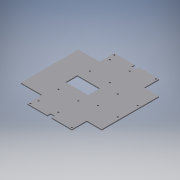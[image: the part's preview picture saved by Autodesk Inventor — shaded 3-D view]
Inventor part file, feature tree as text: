
AUTODESK INVENTOR PART (.ipt)
format: ipt  version: 2016 (Build 200138000, 138)  size: 344,576 bytes
history: native  units: in
note: dims shown in document units (in); Inventor stores cm internally (conversion verified against a paired STEP export)
features: extrude x9, sketch x9
ambient origin geometry x8: Origin, YZ Plane, XZ Plane, XY Plane, X Axis, Y Axis, Z Axis, Center Point
bodies: Solid1 (feature_tree)
feature tree (18):
  extrude  "Extrusion1"  Depth=4.252in
  extrude  "Extrusion4"  Depth=6.4567in
  extrude  "Extrusion5"  Depth=1.1024in
  extrude  "Extrusion6"  Depth=1.4961in
  extrude  "Extrusion7"  Depth=1.4961in
  extrude  "Extrusion9"  Depth=1.5748in
  extrude  "Extrusion12"  Depth=0.315in
  extrude  "Extrusion13"  Depth=0.0787in TaperAngle=0.0deg
  extrude  "Extrusion14"  Depth=0.1969in
  sketch  "Sketch3"  dims[d1=4.252in d2=4.252in]
  sketch  "Sketch9"  dims[d3=6.4567in d4=6.4567in]
  sketch  "Sketch10"  dims[d6=1.1024in d7=1.1024in]
  sketch  "Sketch11"  dims[d11=1.1024in d12=1.4961in]
  sketch  "Sketch12"  dims[d13=1.4961in d14=1.4961in]
  sketch  "Sketch14"  dims[d15=1.4961in d16=1.5748in]
  sketch  "Sketch17"  dims[d18=0.315in d19=0.315in]
  sketch  "Sketch18"  dims[d21=1.1024in d22=0.0787in d23=0.0in]
  sketch  "Sketch19"  dims[d55=0.1181in d56=0.1181in d57=0.1181in d58=0.3937in d59=0.0in d60=1.4685in d61=1.4685in d62=1.4685in d63=1.4685in d64=0.3937in d65=0.1969in d66=0.1969in d67=0.3937in d68=0.1969in d69=0.0in d70=1.4685in d71=1.4685in d72=1.4685in d73=1.4685in d74=0.3937in d75=0.3937in d78=0.1969in d79=0.0in d80=1.4685in d81=1.4685in d82=1.4685in d83=1.4685in d84=0.1969in d85=0.1969in d86=1.3917in d87=1.3917in d88=0.1969in d89=0.0in d105=0.1969in d106=0.1969in d107=0.8661in d108=1.6732in d109=0.3937in d110=0.0in d148=0.5906in d149=0.2756in d150=0.1772in d151=0.2756in d152=0.5906in d153=0.4724in d154=0.5512in d155=0.5906in d156=0.2756in d157=0.4724in d158=0.2756in d159=0.4134in d160=0.3937in d161=0.0in d162=0.2756in d163=0.3937in d164=0.2756in d165=0.3937in d166=0.2756in d167=0.3937in d168=0.3937in d169=0.126in d170=0.1299in d171=0.3937in d172=0.2756in d173=0.3937in d174=0.2756in d175=0.3937in d176=0.0in d177=0.5984in d178=1.1732in d179=0.4528in d180=0.0984in d181=0.5984in d182=1.1732in d183=0.0984in d184=0.4528in d185=0.1181in d186=0.1181in d187=1.1732in d188=0.5984in d189=0.7874in d190=2.0866in d191=0.1969in d192=0.1969in d193=0.1969in d194=0.1969in d195=0.1969in d196=0.1969in d197=0.1969in d198=0.0in d199=0.1969in d200=0.1969in d201=0.1969in d202=0.1969in d203=0.1969in d204=0.1969in d205=0.1969in d206=0.1969in d207=0.1969in d208=0.1969in d209=0.1969in d210=0.1969in]
